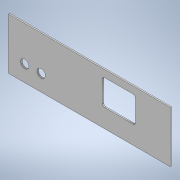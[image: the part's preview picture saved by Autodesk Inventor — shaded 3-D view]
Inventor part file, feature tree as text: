
AUTODESK INVENTOR PART (.ipt)
format: ipt  version: 2021.4 (Build 254397000, 397)  size: 127,488 bytes
history: native  units: in
note: dims shown in document units (in); Inventor stores cm internally (conversion verified against a paired STEP export)
features: extrude x2, sketch x2
ambient origin geometry x8: Origin, YZ Plane, XZ Plane, XY Plane, X Axis, Y Axis, Z Axis, Center Point
bodies: Solid1 (feature_tree)
feature tree (4):
  extrude  "Extrusion1"  Depth=4.9213in
  extrude  "Extrusion2"  Depth=0.1969in
  sketch  "Sketch1"  dims[d0=15.5118in d1=4.9213in]
  sketch  "Sketch2"  dims[d2=0.1181in d3=0.0in d4=0.7874in d6=1.5748in d7=1.5748in d8=1.5748in d9=1.5748in d10=2.4803in d11=0.6693in d12=3.1496in d13=3.3465in d14=0.1181in d15=0.0in d16=0.1969in]
